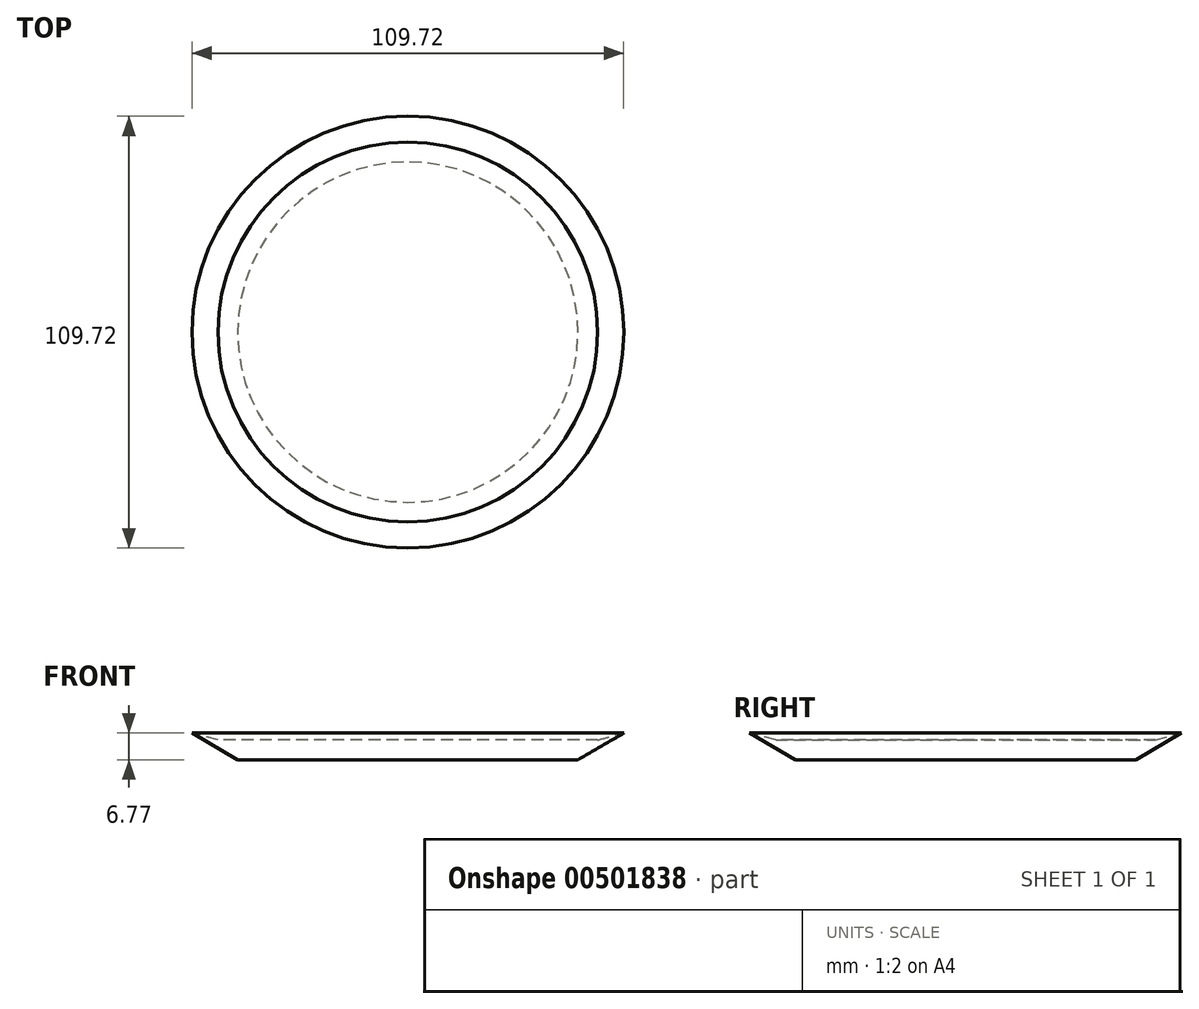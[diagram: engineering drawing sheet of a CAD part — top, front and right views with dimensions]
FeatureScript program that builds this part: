
annotation { "Feature Type Name" : "Feature", "Feature Type Description" : "" }
export const myFeature = defineFeature(function(context is Context, id is Id, definition is map)
    precondition{}
    {
        {
            var Q0;
            Q0=qCreatedBy(makeId("Front.planeOp"),FACE);
            var sketch = newSketch(context, id + "F0", { "sketchPlane" : qUnion([Q0])});
            skLineSegment(sketch, "E0", {"start": v(0, 0) * mm, "end": v(48.24, 0) * mm});
            skLineSegment(sketch, "E1", {"start": v(48.24, 0) * mm, "end": v(54.86, 1.77) * mm});
            skLineSegment(sketch, "E2", {"start": v(54.86, 1.77) * mm, "end": v(43.23, -5) * mm});
            skLineSegment(sketch, "E3", {"start": v(43.23, -5) * mm, "end": v(0, -5) * mm});
            skLineSegment(sketch, "E4", {"start": v(0, -5) * mm, "end": v(0, 0) * mm});
            skLineSegment(sketch, "E5", {"start": v(0, 5.34) * mm, "end": v(0, -22.14) * mm, "construction": true});
            skSolve(sketch);
        }
        {
            var Q0;
            Q0 = qSketchRegion(id + "F0", true);
            var Q1;
            Q1=sQuery(id+"F0.wireOp",EDGE,"E5");
            revolve(context, id + "F1", {"entities" : qUnion([Q0]), "axis" : qUnion([Q1]), "revolveType" : RevolveType.FULL});
        }
    });
